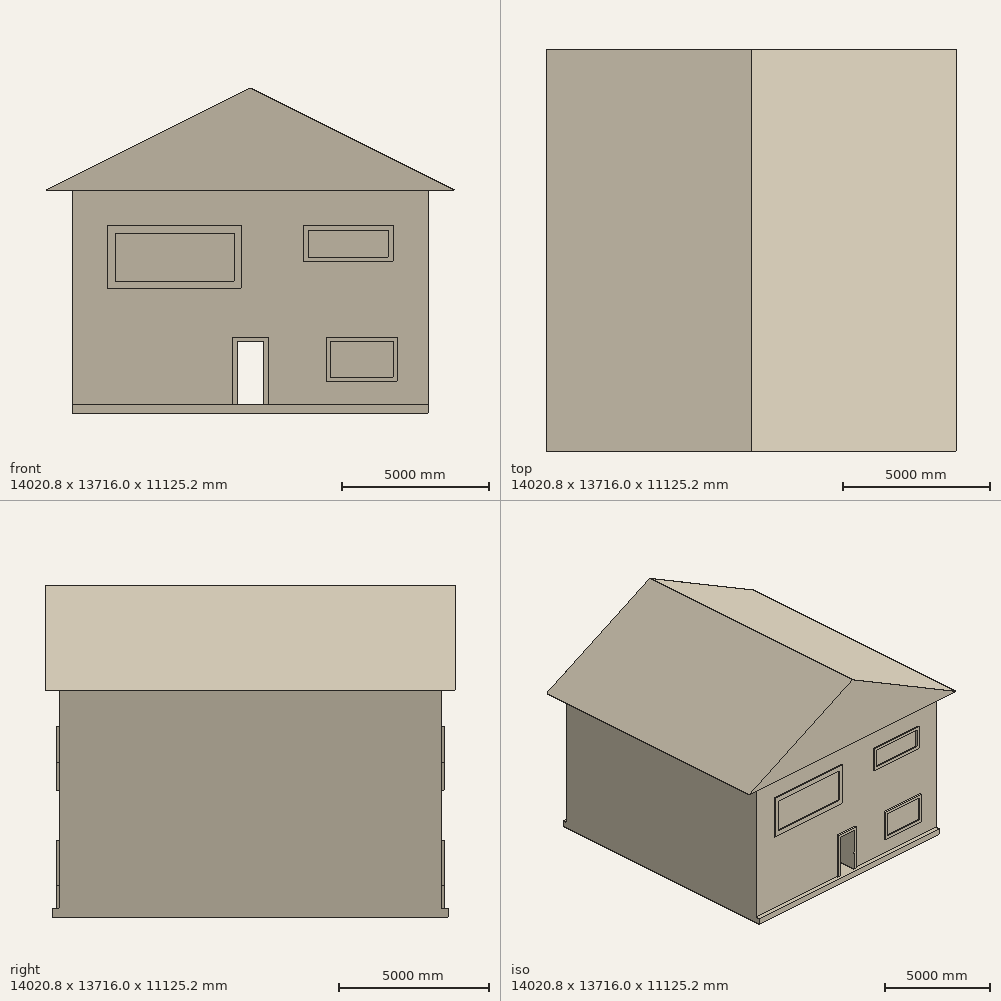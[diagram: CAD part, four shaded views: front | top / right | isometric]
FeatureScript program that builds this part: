
annotation { "Feature Type Name" : "Feature", "Feature Type Description" : "" }
export const myFeature = defineFeature(function(context is Context, id is Id, definition is map)
    precondition{}
    {
        {
            var Q0;
            Q0=qCreatedBy(makeId("Front.planeOp"),FACE);
            var sketch = newSketch(context, id + "F0", { "sketchPlane" : qUnion([Q0])});
            skLineSegment(sketch, "E0", {"start": v(0, 0) * mm, "end": v(-6096, 0) * mm});
            skLineSegment(sketch, "E1", {"start": v(0, 0) * mm, "end": v(6096, 0) * mm});
            skLineSegment(sketch, "E2", {"start": v(6096, 0) * mm, "end": v(0, 0) * mm});
            skLineSegment(sketch, "E3", {"start": v(0, 0) * mm, "end": v(0, 3048) * mm, "construction": true});
            skLineSegment(sketch, "E4", {"start": v(-6096, 0) * mm, "end": v(0, 3048) * mm});
            skLineSegment(sketch, "E5", {"start": v(0, 3048) * mm, "end": v(6096, 0) * mm});
            skLineSegment(sketch, "E6", {"start": v(-6096, 0) * mm, "end": v(-7010.4, 0) * mm});
            skLineSegment(sketch, "E7", {"start": v(6096, 0) * mm, "end": v(7010.4, 0) * mm});
            skLineSegment(sketch, "E8", {"start": v(0, 3048) * mm, "end": v(0, 3505.2) * mm});
            skLineSegment(sketch, "E9", {"start": v(7010.4, 0) * mm, "end": v(0, 3505.2) * mm});
            skLineSegment(sketch, "E10", {"start": v(-7010.4, 0) * mm, "end": v(0, 3505.2) * mm});
            skLineSegment(sketch, "E11", {"start": v(-6096, 0) * mm, "end": v(-6096, -7315.2) * mm});
            skLineSegment(sketch, "E12", {"start": v(-6096, -7315.2) * mm, "end": v(6096, -7315.2) * mm});
            skLineSegment(sketch, "E13", {"start": v(6096, -7315.2) * mm, "end": v(6096, 0) * mm});
            skLineSegment(sketch, "E14", {"start": v(-6096, -7315.2) * mm, "end": v(-6096, -7620) * mm});
            skLineSegment(sketch, "E15", {"start": v(-6096, -7620) * mm, "end": v(6096, -7620) * mm});
            skLineSegment(sketch, "E16", {"start": v(6096, -7620) * mm, "end": v(6096, -7315.2) * mm});
            skLineSegment(sketch, "E17", {"start": v(0, -7315.2) * mm, "end": v(-457.2, -7315.2) * mm});
            skLineSegment(sketch, "E18", {"start": v(-457.2, -7315.2) * mm, "end": v(-457.2, -5181.6) * mm});
            skLineSegment(sketch, "E19", {"start": v(-457.2, -5181.6) * mm, "end": v(457.2, -5181.6) * mm});
            skLineSegment(sketch, "E20", {"start": v(457.2, -5181.6) * mm, "end": v(457.2, -7315.2) * mm});
            skLineSegment(sketch, "E21", {"start": v(457.2, -7315.2) * mm, "end": v(0, -7315.2) * mm});
            skLineSegment(sketch, "E22.bottom", {"start": v(2743.2, -5181.6) * mm, "end": v(4876.8, -5181.6) * mm});
            skLineSegment(sketch, "E22.top", {"start": v(2743.2, -6400.8) * mm, "end": v(4876.8, -6400.8) * mm});
            skLineSegment(sketch, "E22.left", {"start": v(2743.2, -5181.6) * mm, "end": v(2743.2, -6400.8) * mm});
            skLineSegment(sketch, "E22.right", {"start": v(4876.8, -5181.6) * mm, "end": v(4876.8, -6400.8) * mm});
            skLineSegment(sketch, "E23.bottom", {"start": v(1828.8, -1219.2) * mm, "end": v(4876.8, -1219.2) * mm});
            skLineSegment(sketch, "E23.top", {"start": v(1828.8, -2438.4) * mm, "end": v(4876.8, -2438.4) * mm});
            skLineSegment(sketch, "E23.left", {"start": v(1828.8, -1219.2) * mm, "end": v(1828.8, -2438.4) * mm});
            skLineSegment(sketch, "E23.right", {"start": v(4876.8, -1219.2) * mm, "end": v(4876.8, -2438.4) * mm});
            skLineSegment(sketch, "E24.bottom", {"start": v(-4876.8, -1219.2) * mm, "end": v(-304.8, -1219.2) * mm});
            skLineSegment(sketch, "E24.top", {"start": v(-4876.8, -3352.8) * mm, "end": v(-304.8, -3352.8) * mm});
            skLineSegment(sketch, "E24.left", {"start": v(-4876.8, -1219.2) * mm, "end": v(-4876.8, -3352.8) * mm});
            skLineSegment(sketch, "E24.right", {"start": v(-304.8, -1219.2) * mm, "end": v(-304.8, -3352.8) * mm});
            skLineSegment(sketch, "E25.0", {"start": v(1981.2, -1371.6) * mm, "end": v(4724.4, -1371.6) * mm});
            skLineSegment(sketch, "E25.1", {"start": v(1981.2, -1371.6) * mm, "end": v(1981.2, -2286) * mm});
            skLineSegment(sketch, "E25.2", {"start": v(1981.2, -2286) * mm, "end": v(4724.4, -2286) * mm});
            skLineSegment(sketch, "E25.3", {"start": v(4724.4, -1371.6) * mm, "end": v(4724.4, -2286) * mm});
            skLineSegment(sketch, "E26.0", {"start": v(2590.8, -5029.2) * mm, "end": v(5029.2, -5029.2) * mm});
            skLineSegment(sketch, "E26.1", {"start": v(2590.8, -5029.2) * mm, "end": v(2590.8, -6553.2) * mm});
            skLineSegment(sketch, "E26.2", {"start": v(2590.8, -6553.2) * mm, "end": v(5029.2, -6553.2) * mm});
            skLineSegment(sketch, "E26.3", {"start": v(5029.2, -5029.2) * mm, "end": v(5029.2, -6553.2) * mm});
            skLineSegment(sketch, "E27.0", {"start": v(-4632.96, -1463.04) * mm, "end": v(-548.64, -1463.04) * mm});
            skLineSegment(sketch, "E27.1", {"start": v(-4632.96, -1463.04) * mm, "end": v(-4632.96, -3108.96) * mm});
            skLineSegment(sketch, "E27.2", {"start": v(-4632.96, -3108.96) * mm, "end": v(-548.64, -3108.96) * mm});
            skLineSegment(sketch, "E27.3", {"start": v(-548.64, -1463.04) * mm, "end": v(-548.64, -3108.96) * mm});
            skLineSegment(sketch, "E28.0", {"start": v(609.6, -5029.2) * mm, "end": v(609.6, -7315.2) * mm});
            skLineSegment(sketch, "E28.1", {"start": v(-609.6, -5029.2) * mm, "end": v(609.6, -5029.2) * mm});
            skLineSegment(sketch, "E28.2", {"start": v(-609.6, -7315.2) * mm, "end": v(-609.6, -5029.2) * mm});
            skSolve(sketch);
        }
        {
            var Q0;
            Q0=makeQuery(id+"F0.imprint","IMPRINT",FACE,{"disambiguationData":[TD([[makeQuery(id+"F0.imprint","IMPRINT",EDGE,{"derivedFrom":sQuery(id+"F0.wireOp",EDGE,"E4")}),1.0]])]});
            var Q1;
            Q1=makeQuery(id+"F0.imprint","IMPRINT",FACE,{"disambiguationData":[TD([[makeQuery(id+"F0.imprint","IMPRINT",EDGE,{"derivedFrom":sQuery(id+"F0.wireOp",EDGE,"E5")}),1.0]])]});
            extrude(context, id + "F1", {"entities" : qUnion([Q0, Q1]), "endBound" : BoundingType.SYMMETRIC, "depth" : 13716 * mm, "offsetDistance" : 30.48 * mm});
        }
        {
            var Q0;
            Q0=makeQuery(id+"F0.imprint","IMPRINT",FACE,{"disambiguationData":[TD([[makeQuery(id+"F0.imprint","IMPRINT",EDGE,{"derivedFrom":sQuery(id+"F0.wireOp",EDGE,"E0")}),-1.0]])]});
            extrude(context, id + "F2", {"entities" : qUnion([Q0]), "operationType" : NewBodyOperationType.ADD, "endBound" : BoundingType.SYMMETRIC, "depth" : 13716 * mm, "offsetDistance" : 30.48 * mm});
        }
        {
            var Q0;
            Q0=makeQuery(id+"F0.imprint","IMPRINT",FACE,{"disambiguationData":[TD([[makeQuery(id+"F0.imprint","IMPRINT",EDGE,{"derivedFrom":sQuery(id+"F0.wireOp",EDGE,"E0")}),1.0]])]});
            extrude(context, id + "F3", {"entities" : qUnion([Q0]), "operationType" : NewBodyOperationType.ADD, "endBound" : BoundingType.SYMMETRIC, "depth" : 12801.6 * mm, "offsetDistance" : 30.48 * mm});
        }
        {
            var Q0;
            Q0=makeQuery(id+"F0.imprint","IMPRINT",FACE,{"disambiguationData":[TD([[makeQuery(id+"F0.imprint","IMPRINT",EDGE,{"derivedFrom":sQuery(id+"F0.wireOp",EDGE,"E24.bottom")}),-1.0]])]});
            var Q1;
            Q1=makeQuery(id+"F0.imprint","IMPRINT",FACE,{"disambiguationData":[TD([[makeQuery(id+"F0.imprint","IMPRINT",EDGE,{"derivedFrom":sQuery(id+"F0.wireOp",EDGE,"E23.bottom")}),-1.0]])]});
            var Q2;
            {var subQ0=sQuery(id+"F0.wireOp",EDGE,"E18");Q2=makeQuery(id+"F0.imprint","IMPRINT",FACE,{"disambiguationData":[TD([[makeQuery(id+"F0.imprint","IMPRINT",EDGE,{"derivedFrom":subQ0}),1.0]])]});}
            var Q3;
            Q3=makeQuery(id+"F0.imprint","IMPRINT",FACE,{"disambiguationData":[TD([[makeQuery(id+"F0.imprint","IMPRINT",EDGE,{"derivedFrom":sQuery(id+"F0.wireOp",EDGE,"E22.bottom")}),1.0]])]});
            extrude(context, id + "F4", {"entities" : qUnion([Q0, Q1, Q2, Q3]), "operationType" : NewBodyOperationType.ADD, "endBound" : BoundingType.SYMMETRIC, "depth" : 12954 * mm, "offsetDistance" : 30.48 * mm});
        }
        {
            var Q0;
            {var subQ6=sQuery(id+"F0.wireOp",EDGE,"E14");Q0=makeQuery(id+"F0.imprint","IMPRINT",FACE,{"disambiguationData":[TD([[makeQuery(id+"F0.imprint","IMPRINT",EDGE,{"derivedFrom":subQ6}),1.0]])]});}
            extrude(context, id + "F5", {"entities" : qUnion([Q0]), "operationType" : NewBodyOperationType.ADD, "endBound" : BoundingType.SYMMETRIC, "depth" : 13258.8 * mm, "offsetDistance" : 30.48 * mm});
        }
        {
            var Q0;
            Q0=makeQuery(id+"F0.imprint","IMPRINT",FACE,{"disambiguationData":[TD([[makeQuery(id+"F0.imprint","IMPRINT",EDGE,{"derivedFrom":sQuery(id+"F0.wireOp",EDGE,"E27.0")}),-1.0]])]});
            var Q1;
            Q1=makeQuery(id+"F0.imprint","IMPRINT",FACE,{"disambiguationData":[TD([[makeQuery(id+"F0.imprint","IMPRINT",EDGE,{"derivedFrom":sQuery(id+"F0.wireOp",EDGE,"E25.0")}),-1.0]])]});
            var Q2;
            Q2=makeQuery(id+"F0.imprint","IMPRINT",FACE,{"disambiguationData":[TD([[makeQuery(id+"F0.imprint","IMPRINT",EDGE,{"derivedFrom":sQuery(id+"F0.wireOp",EDGE,"E22.bottom")}),-1.0]])]});
            var Q3;
            Q3=makeQuery(id+"F0.imprint","IMPRINT",FACE,{"disambiguationData":[TD([[makeQuery(id+"F0.imprint","IMPRINT",EDGE,{"derivedFrom":sQuery(id+"F0.wireOp",EDGE,"E17")}),-1.0]])]});
            extrude(context, id + "F6", {"entities" : qUnion([Q0, Q1, Q2, Q3]), "operationType" : NewBodyOperationType.ADD, "endBound" : BoundingType.SYMMETRIC, "depth" : 12801.6 * mm, "offsetDistance" : 30.48 * mm});
        }
    });
